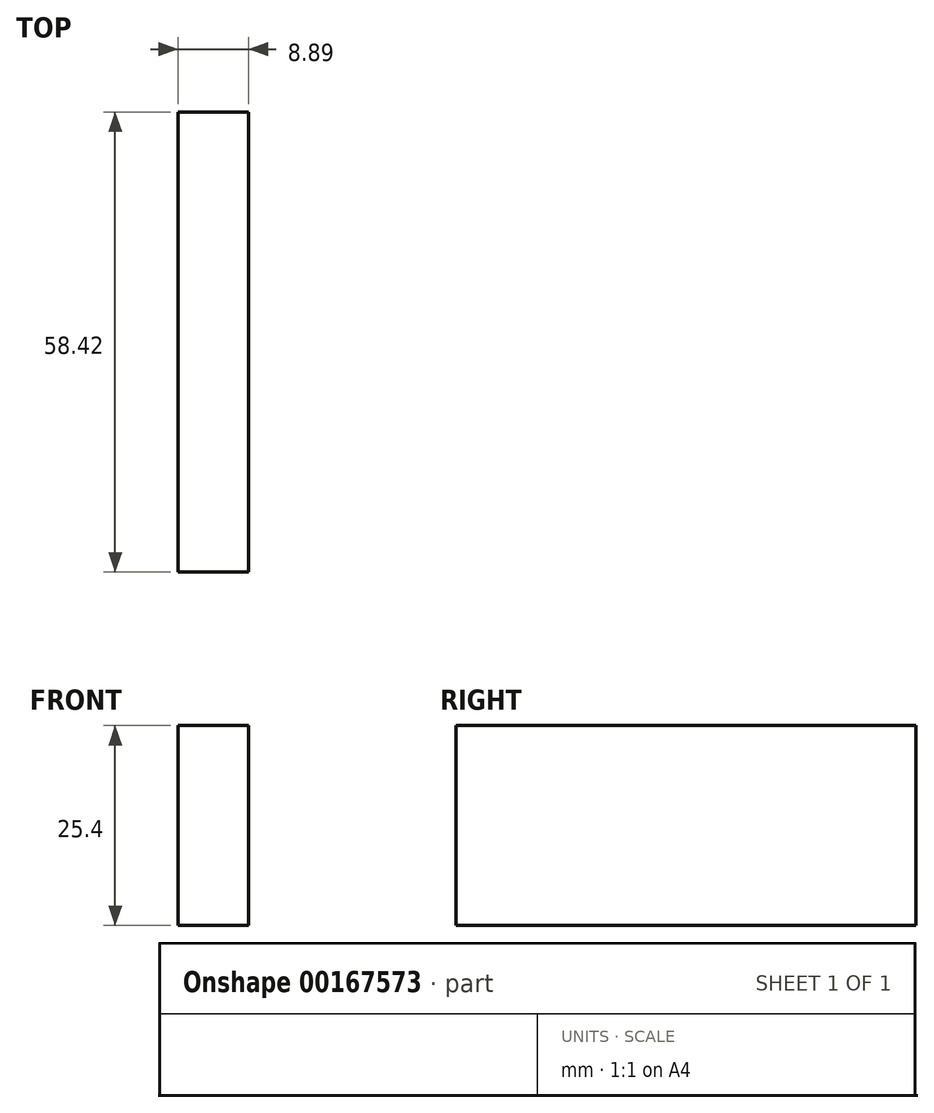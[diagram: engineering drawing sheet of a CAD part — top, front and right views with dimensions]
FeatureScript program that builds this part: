
annotation { "Feature Type Name" : "Feature", "Feature Type Description" : "" }
export const myFeature = defineFeature(function(context is Context, id is Id, definition is map)
    precondition{}
    {
        {
            var Q0;
            Q0=qCreatedBy(makeId("Right.planeOp"),FACE);
            var sketch = newSketch(context, id + "F0", { "sketchPlane" : qUnion([Q0])});
            skLineSegment(sketch, "E0.bottom", {"start": v(0, 0) * mm, "end": v(58.42, 0) * mm});
            skLineSegment(sketch, "E0.top", {"start": v(0, 25.4) * mm, "end": v(58.42, 25.4) * mm});
            skLineSegment(sketch, "E0.left", {"start": v(0, 0) * mm, "end": v(0, 25.4) * mm});
            skLineSegment(sketch, "E0.right", {"start": v(58.42, 0) * mm, "end": v(58.42, 25.4) * mm});
            skSolve(sketch);
        }
        {
            var Q0;
            Q0 = qSketchRegion(id + "F0", true);
            extrude(context, id + "F1", {"entities" : qUnion([Q0]), "depth" : 8.9 * mm});
        }
    });
